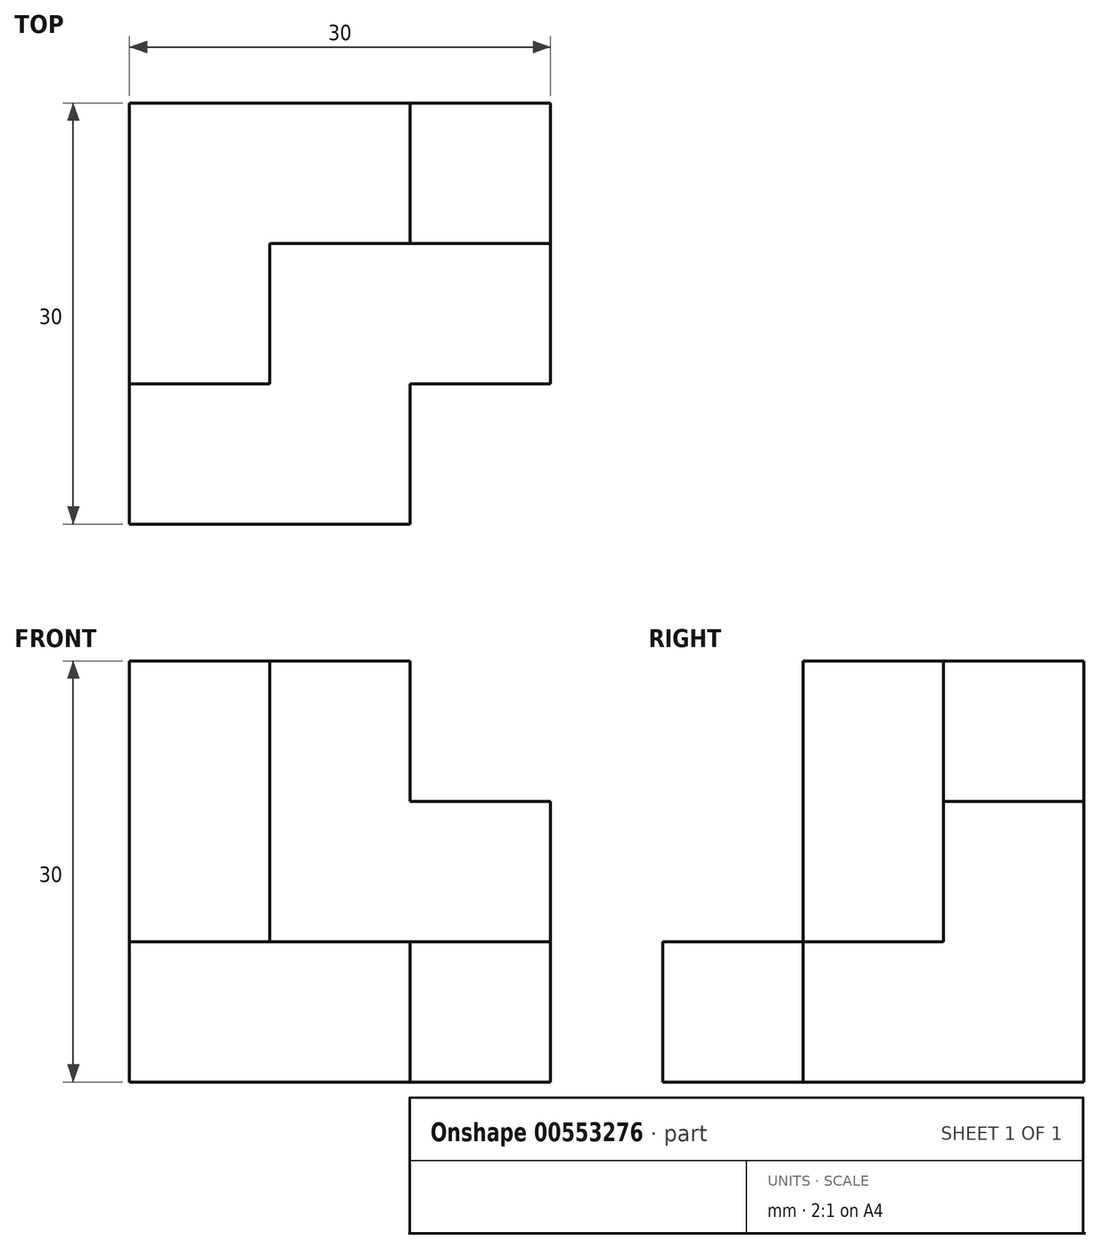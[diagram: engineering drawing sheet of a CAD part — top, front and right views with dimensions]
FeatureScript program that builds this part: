
annotation { "Feature Type Name" : "Feature", "Feature Type Description" : "" }
export const myFeature = defineFeature(function(context is Context, id is Id, definition is map)
    precondition{}
    {
        {
            var Q0;
            Q0=qCreatedBy(makeId("Top.planeOp"),FACE);
            var sketch = newSketch(context, id + "F0", { "sketchPlane" : qUnion([Q0])});
            skLineSegment(sketch, "E0.bottom", {"start": v(0, 0) * mm, "end": v(30, 0) * mm});
            skLineSegment(sketch, "E0.top", {"start": v(0, 30) * mm, "end": v(30, 30) * mm});
            skLineSegment(sketch, "E0.left", {"start": v(0, 0) * mm, "end": v(0, 30) * mm});
            skLineSegment(sketch, "E0.right", {"start": v(30, 0) * mm, "end": v(30, 30) * mm});
            skSolve(sketch);
        }
        {
            var Q0;
            Q0=qSketchRegion(id+"F0",true);
            extrude(context, id + "F1", {"entities" : qUnion([Q0]), "depth" : 30 * mm, "offsetDistance" : 25 * mm});
        }
        {
            var Q0;
            Q0=makeQuery(id+"F1.opExtrude","CAP_FACE",FACE,{"disambiguationData":[OSD([sQuery(id+"F0.wireOp",EDGE,"E0.bottom"),sQuery(id+"F0.wireOp",EDGE,"E0.top"),sQuery(id+"F0.wireOp",EDGE,"E0.left"),sQuery(id+"F0.wireOp",EDGE,"E0.right")])],"isStart":false});
            var sketch = newSketch(context, id + "F2", { "sketchPlane" : qUnion([Q0])});
            skLineSegment(sketch, "E1", {"start": v(0, 10) * mm, "end": v(10, 10) * mm});
            skLineSegment(sketch, "E2", {"start": v(10, 10) * mm, "end": v(10, 20) * mm});
            skLineSegment(sketch, "E3", {"start": v(10, 20) * mm, "end": v(30, 20) * mm});
            skSolve(sketch);
        }
        {
            var Q0;
            {var subQ2=sQuery(id+"F2.wireOp",EDGE,"E1");Q0=makeQuery(id+"F2.imprint","IMPRINT",FACE,{"disambiguationData":[TD([[makeQuery(id+"F2.imprint","IMPRINT",EDGE,{"derivedFrom":subQ2}),-1.0]])]});}
            extrude(context, id + "F3", {"entities" : qUnion([Q0]), "operationType" : NewBodyOperationType.REMOVE, "oppositeDirection" : true, "depth" : 20 * mm, "offsetDistance" : 25 * mm});
        }
        {
            var Q0;
            Q0=makeQuery(id+"F3.boolean.opBoolean","COPY",FACE,{"derivedFrom":makeQuery(id+"F3.opExtrude","SWEPT_FACE",FACE,{"disambiguationData":[OSD([sQuery(id+"F2.wireOp",EDGE,"E3")])]})});
            var sketch = newSketch(context, id + "F4", { "sketchPlane" : qUnion([Q0])});
            skLineSegment(sketch, "E4.bottom", {"start": v(30, 30) * mm, "end": v(20, 30) * mm});
            skLineSegment(sketch, "E4.top", {"start": v(30, 20) * mm, "end": v(20, 20) * mm});
            skLineSegment(sketch, "E4.left", {"start": v(30, 30) * mm, "end": v(30, 20) * mm});
            skLineSegment(sketch, "E4.right", {"start": v(20, 30) * mm, "end": v(20, 20) * mm});
            skSolve(sketch);
        }
        {
            var Q0;
            Q0 = qSketchRegion(id + "F4", true);
            extrude(context, id + "F5", {"entities" : qUnion([Q0]), "operationType" : NewBodyOperationType.REMOVE, "endBound" : BoundingType.THROUGH_ALL, "oppositeDirection" : true, "depth" : 25 * mm, "offsetDistance" : 25 * mm});
        }
        {
            var Q0;
            Q0=makeQuery(id+"F3.boolean.opBoolean","COPY",FACE,{"derivedFrom":makeQuery(id+"F3.opExtrude","CAP_FACE",FACE,{"disambiguationData":[OSD([sQuery(id+"F0.wireOp",EDGE,"E0.bottom"),sQuery(id+"F0.wireOp",EDGE,"E0.left"),sQuery(id+"F0.wireOp",EDGE,"E0.right"),sQuery(id+"F2.wireOp",EDGE,"E1"),sQuery(id+"F2.wireOp",EDGE,"E2"),sQuery(id+"F2.wireOp",EDGE,"E3")])],"isStart":false})});
            var sketch = newSketch(context, id + "F6", { "sketchPlane" : qUnion([Q0])});
            skLineSegment(sketch, "E5.bottom", {"start": v(30, 0) * mm, "end": v(20, 0) * mm});
            skLineSegment(sketch, "E5.top", {"start": v(30, 10) * mm, "end": v(20, 10) * mm});
            skLineSegment(sketch, "E5.left", {"start": v(30, 0) * mm, "end": v(30, 10) * mm});
            skLineSegment(sketch, "E5.right", {"start": v(20, 0) * mm, "end": v(20, 10) * mm});
            skSolve(sketch);
        }
        {
            var Q0;
            Q0 = qSketchRegion(id + "F6", true);
            extrude(context, id + "F7", {"entities" : qUnion([Q0]), "operationType" : NewBodyOperationType.REMOVE, "endBound" : BoundingType.THROUGH_ALL, "oppositeDirection" : true, "depth" : 25 * mm, "offsetDistance" : 25 * mm});
        }
    });
